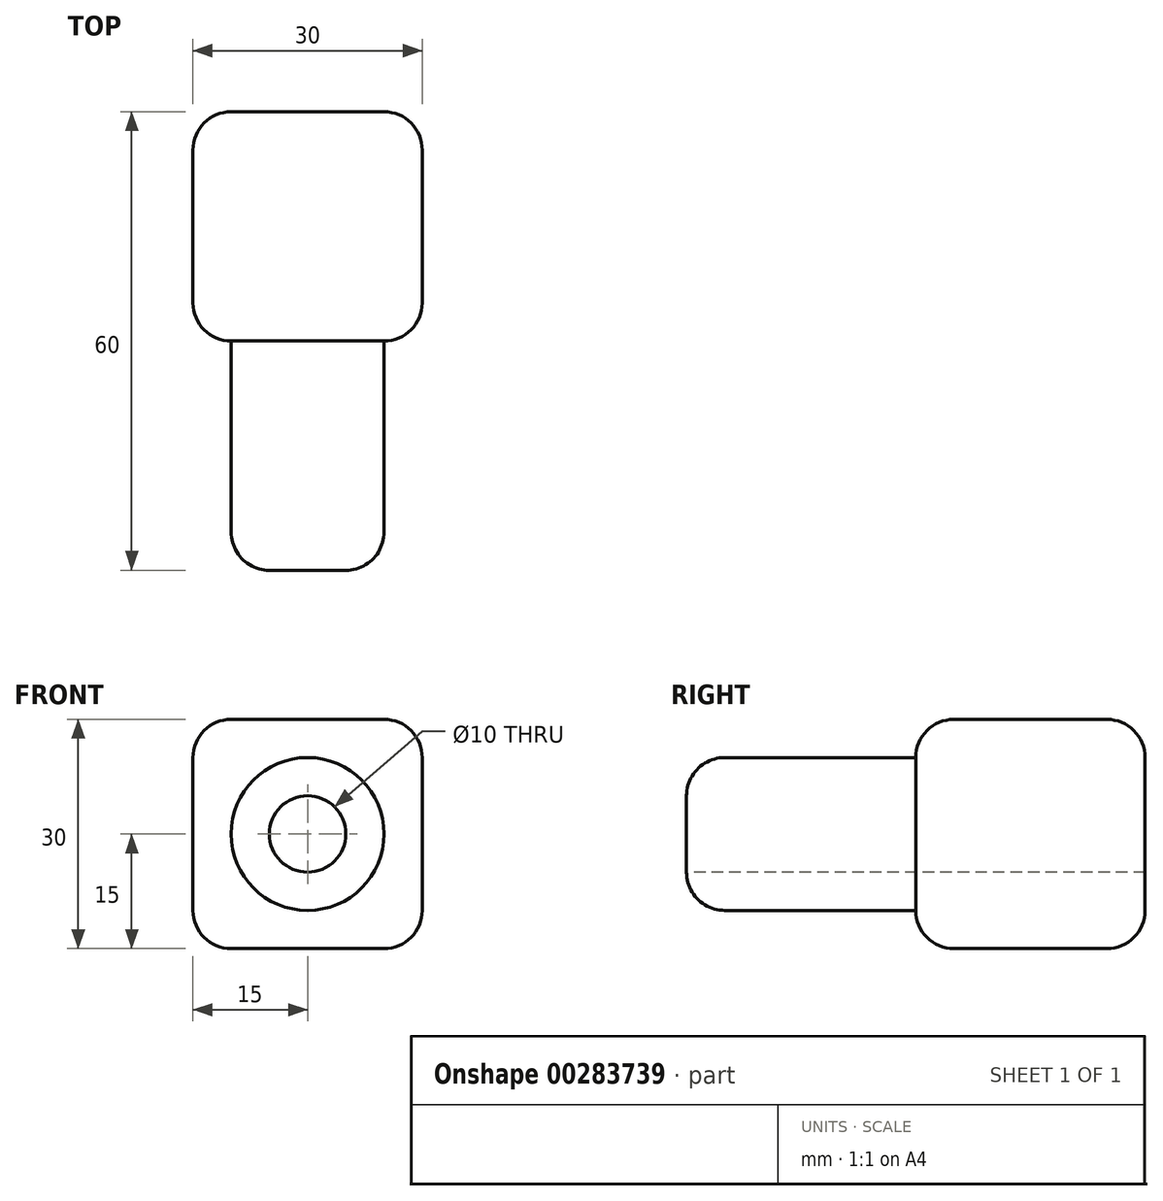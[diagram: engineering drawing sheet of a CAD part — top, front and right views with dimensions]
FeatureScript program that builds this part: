
annotation { "Feature Type Name" : "Feature", "Feature Type Description" : "" }
export const myFeature = defineFeature(function(context is Context, id is Id, definition is map)
    precondition{}
    {
        {
            var Q0;
            Q0=qCreatedBy(makeId("Front.planeOp"),FACE);
            var sketch = newSketch(context, id + "F0", { "sketchPlane" : qUnion([Q0])});
            skLineSegment(sketch, "E0.bottom", {"start": v(15, 15) * mm, "end": v(-15, 15) * mm});
            skLineSegment(sketch, "E0.top", {"start": v(15, -15) * mm, "end": v(-15, -15) * mm});
            skLineSegment(sketch, "E0.left", {"start": v(15, 15) * mm, "end": v(15, -15) * mm});
            skLineSegment(sketch, "E0.right", {"start": v(-15, 15) * mm, "end": v(-15, -15) * mm});
            skPoint(sketch, "E0.middle", {"position": v(0, 0) * mm});
            skSolve(sketch);
        }
        {
            var Q0;
            Q0 = qSketchRegion(id + "F0", true);
            extrude(context, id + "F1", {"entities" : qUnion([Q0]), "depth" : 30 * mm});
        }
        {
            var Q0;
            Q0=makeQuery(id+"F1.opExtrude","CAP_FACE",FACE,{"disambiguationData":[OSD([sQuery(id+"F0.wireOp",EDGE,"E0.bottom"),sQuery(id+"F0.wireOp",EDGE,"E0.top"),sQuery(id+"F0.wireOp",EDGE,"E0.left"),sQuery(id+"F0.wireOp",EDGE,"E0.right")])],"isStart":false});
            var sketch = newSketch(context, id + "F2", { "sketchPlane" : qUnion([Q0])});
            skCircle(sketch, "E1", {"center": v(0, 0) * mm, "radius": 10 * mm});
            skSolve(sketch);
        }
        {
            var Q0;
            Q0 = qSketchRegion(id + "F2", true);
            extrude(context, id + "F3", {"entities" : qUnion([Q0]), "operationType" : NewBodyOperationType.ADD, "depth" : 30 * mm});
        }
        {
            var Q0;
            Q0=makeQuery(id+"F3.opExtrude","CAP_FACE",FACE,{"disambiguationData":[OSD([sQuery(id+"F2.wireOp",EDGE,"E1")])],"isStart":false});
            var sketch = newSketch(context, id + "F4", { "sketchPlane" : qUnion([Q0])});
            skCircle(sketch, "E2", {"center": v(0, 0) * mm, "radius": 5 * mm});
            skSolve(sketch);
        }
        {
            var Q0;
            Q0 = qSketchRegion(id + "F4", true);
            extrude(context, id + "F5", {"entities" : qUnion([Q0]), "operationType" : NewBodyOperationType.REMOVE, "endBound" : BoundingType.THROUGH_ALL, "oppositeDirection" : true, "depth" : 25 * mm});
        }
        {
            var Q0;
            Q0=makeQuery(id+"F1.opExtrude","CAP_EDGE",EDGE,{"disambiguationData":[OSD([sQuery(id+"F0.wireOp",EDGE,"E0.bottom")])],"isStart":false});
            var Q1;
            Q1=makeQuery(id+"F1.opExtrude","CAP_EDGE",EDGE,{"disambiguationData":[OSD([sQuery(id+"F0.wireOp",EDGE,"E0.right")])],"isStart":false});
            var Q2;
            Q2=makeQuery(id+"F1.opExtrude","CAP_EDGE",EDGE,{"disambiguationData":[OSD([sQuery(id+"F0.wireOp",EDGE,"E0.left")])],"isStart":false});
            var Q3;
            Q3=makeQuery(id+"F1.opExtrude","CAP_EDGE",EDGE,{"disambiguationData":[OSD([sQuery(id+"F0.wireOp",EDGE,"E0.top")])],"isStart":false});
            var Q4;
            Q4=makeQuery(id+"F1.opExtrude","SWEPT_EDGE",EDGE,{"disambiguationData":[OSD([sQuery(id+"F0.wireOp",EDGE,"E0.bottom"),sQuery(id+"F0.wireOp",EDGE,"E0.left")])]});
            var Q5;
            Q5=makeQuery(id+"F1.opExtrude","SWEPT_EDGE",EDGE,{"disambiguationData":[OSD([sQuery(id+"F0.wireOp",EDGE,"E0.top"),sQuery(id+"F0.wireOp",EDGE,"E0.left")])]});
            var Q6;
            Q6=makeQuery(id+"F1.opExtrude","CAP_EDGE",EDGE,{"disambiguationData":[OSD([sQuery(id+"F0.wireOp",EDGE,"E0.left")])],"isStart":true});
            var Q7;
            Q7=makeQuery(id+"F1.opExtrude","CAP_EDGE",EDGE,{"disambiguationData":[OSD([sQuery(id+"F0.wireOp",EDGE,"E0.bottom")])],"isStart":true});
            var Q8;
            Q8=makeQuery(id+"F1.opExtrude","SWEPT_EDGE",EDGE,{"disambiguationData":[OSD([sQuery(id+"F0.wireOp",EDGE,"E0.bottom"),sQuery(id+"F0.wireOp",EDGE,"E0.right")])]});
            var Q9;
            Q9=makeQuery(id+"F1.opExtrude","CAP_EDGE",EDGE,{"disambiguationData":[OSD([sQuery(id+"F0.wireOp",EDGE,"E0.top")])],"isStart":true});
            var Q10;
            Q10=makeQuery(id+"F1.opExtrude","CAP_EDGE",EDGE,{"disambiguationData":[OSD([sQuery(id+"F0.wireOp",EDGE,"E0.right")])],"isStart":true});
            var Q11;
            Q11=makeQuery(id+"F3.opExtrude","CAP_EDGE",EDGE,{"disambiguationData":[OSD([sQuery(id+"F2.wireOp",EDGE,"E1")])],"isStart":false});
            fillet(context, id + "F6", {"entities" : qUnion([Q0, Q1, Q2, Q3, Q4, Q5, Q6, Q7, Q8, Q9, Q10, Q11]), "radius" : 5 * mm, "tangentPropagation" : true, "allowEdgeOverflow" : false});
        }
        {
            var Q0;
            Q0=makeQuery(id+"F1.opExtrude","SWEPT_EDGE",EDGE,{"disambiguationData":[OSD([sQuery(id+"F0.wireOp",EDGE,"E0.top"),sQuery(id+"F0.wireOp",EDGE,"E0.right")])]});
            var Q1;
            {var subQ0=sQuery(id+"F0.wireOp",EDGE,"E0.right");Q1=makeQuery(id+"F6.opFillet","BLEND_EDGE",EDGE,{"blendedFrom":[makeQuery(id+"F1.opExtrude","SWEPT_EDGE",EDGE,{"disambiguationData":[OSD([sQuery(id+"F0.wireOp",EDGE,"E0.bottom"),subQ0])]}),makeQuery(id+"F1.opExtrude","SWEPT_FACE",FACE,{"disambiguationData":[OSD([subQ0])]})],"blendedInto":[makeQuery(id+"F1.opExtrude","SWEPT_FACE",FACE,{"disambiguationData":[OSD([subQ0])]})]});}
            fillet(context, id + "F7", {"entities" : qUnion([Q0, Q1]), "radius" : 5 * mm, "tangentPropagation" : true, "allowEdgeOverflow" : false});
        }
    });
